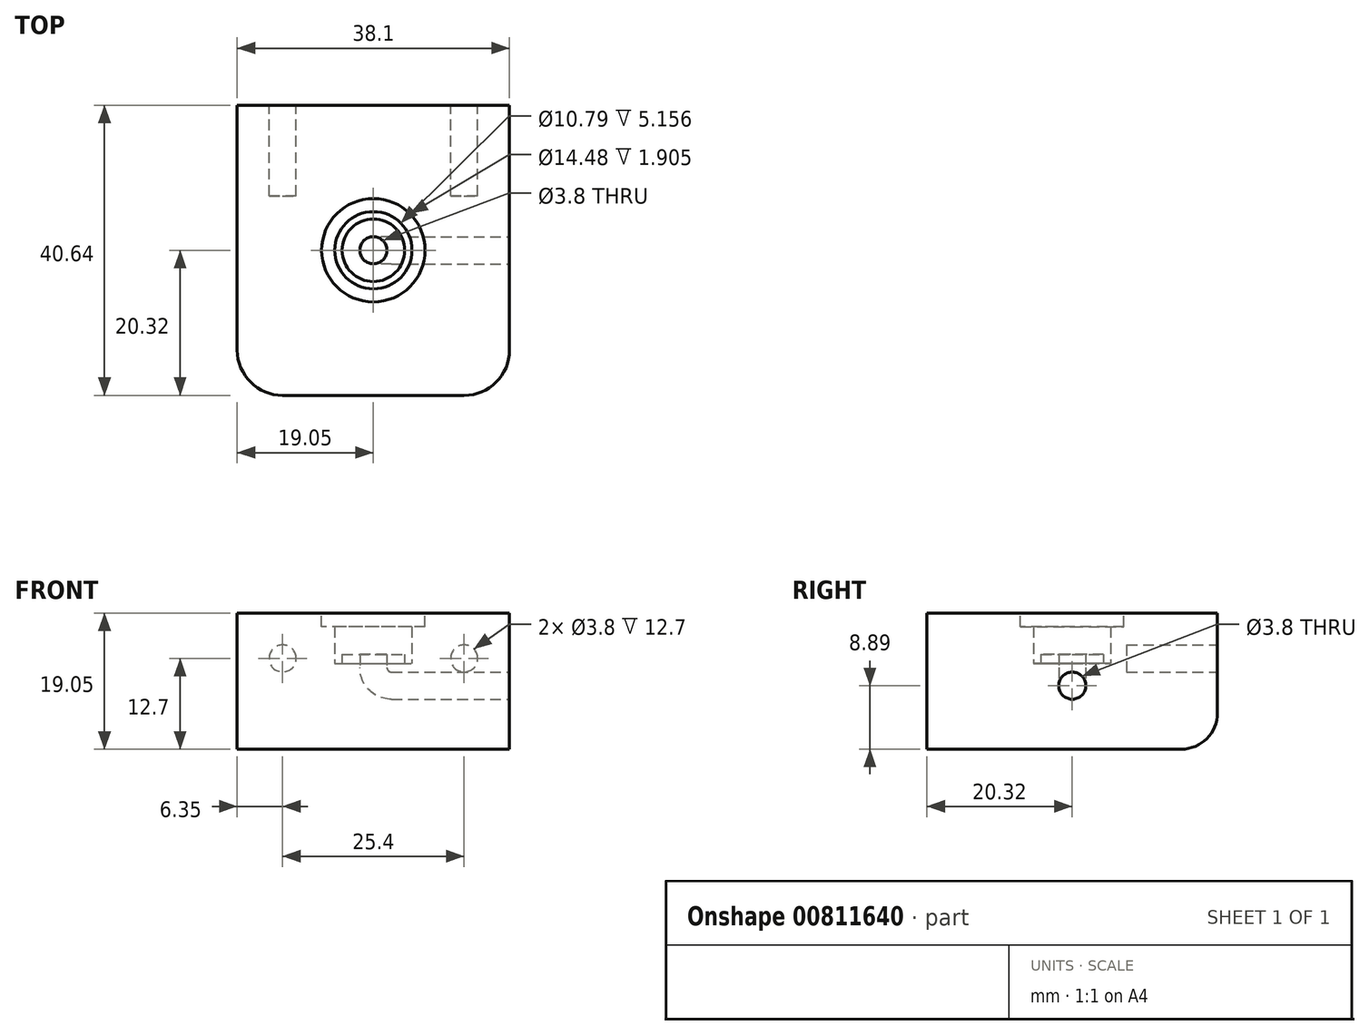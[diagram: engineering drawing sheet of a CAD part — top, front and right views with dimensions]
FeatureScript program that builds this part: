
annotation { "Feature Type Name" : "Feature", "Feature Type Description" : "" }
export const myFeature = defineFeature(function(context is Context, id is Id, definition is map)
    precondition{}
    {
        {
            var Q0;
            Q0=qCreatedBy(makeId("Top.planeOp"),FACE);
            var sketch = newSketch(context, id + "F0", { "sketchPlane" : qUnion([Q0])});
            skLineSegment(sketch, "E0.bottom", {"start": v(19.05, -20.32) * mm, "end": v(-19.05, -20.32) * mm});
            skLineSegment(sketch, "E0.top", {"start": v(19.05, 20.32) * mm, "end": v(-19.05, 20.32) * mm});
            skLineSegment(sketch, "E0.left", {"start": v(19.05, -20.32) * mm, "end": v(19.05, 20.32) * mm});
            skLineSegment(sketch, "E0.right", {"start": v(-19.05, -20.32) * mm, "end": v(-19.05, 20.32) * mm});
            skPoint(sketch, "E0.middle", {"position": v(0, 0) * mm});
            skSolve(sketch);
        }
        {
            var Q0;
            Q0 = qSketchRegion(id + "F0", true);
            extrude(context, id + "F1", {"entities" : qUnion([Q0]), "oppositeDirection" : true, "depth" : 19.05 * mm, "offsetDistance" : 25.4 * mm});
        }
        {
            var Q0;
            Q0=qCreatedBy(makeId("Front.planeOp"),FACE);
            var sketch = newSketch(context, id + "F2", { "sketchPlane" : qUnion([Q0])});
            skLineSegment(sketch, "E1", {"start": v(0, 0) * mm, "end": v(0, -19.05) * mm, "construction": true});
            skLineSegment(sketch, "E2.0", {"start": v(19.05, -19.05) * mm, "end": v(-19.05, -19.05) * mm, "construction": true});
            skLineSegment(sketch, "E3", {"start": v(0, 0) * mm, "end": v(0, -5.8) * mm});
            skLineSegment(sketch, "E4", {"start": v(0, -5.8) * mm, "end": v(4.38, -5.8) * mm});
            skLineSegment(sketch, "E5", {"start": v(4.38, -5.8) * mm, "end": v(4.38, -7.06) * mm});
            skLineSegment(sketch, "E6", {"start": v(4.38, -7.06) * mm, "end": v(5.4, -7.06) * mm});
            skLineSegment(sketch, "E7", {"start": v(5.4, -7.06) * mm, "end": v(5.4, 0) * mm});
            skLineSegment(sketch, "E8", {"start": v(5.4, 0) * mm, "end": v(0, 0) * mm});
            skLineSegment(sketch, "E9", {"start": v(0, -5.8) * mm, "end": v(0, 0) * mm});
            skSolve(sketch);
        }
        {
            var Q0;
            Q0=makeQuery(id+"F2.imprint","IMPRINT",FACE,{"disambiguationData":[TD([[makeQuery(id+"F2.imprint","IMPRINT",EDGE,{"derivedFrom":sQuery(id+"F2.wireOp",EDGE,"E4")}),1.0]])]});
            var Q1;
            Q1=sQuery(id+"F2.wireOp",EDGE,"E1");
            revolve(context, id + "F3", {"operationType" : NewBodyOperationType.REMOVE, "surfaceOperationType" : NewSurfaceOperationType.NEW, "entities" : qUnion([Q0]), "axis" : qUnion([Q1]), "revolveType" : RevolveType.FULL, "oppositeDirection" : true});
        }
        {
            var Q0;
            Q0=makeQuery(id+"F1.opExtrude","CAP_FACE",FACE,{"disambiguationData":[OSD([sQuery(id+"F0.wireOp",EDGE,"E0.bottom"),sQuery(id+"F0.wireOp",EDGE,"E0.top"),sQuery(id+"F0.wireOp",EDGE,"E0.left"),sQuery(id+"F0.wireOp",EDGE,"E0.right")])],"isStart":true});
            var sketch = newSketch(context, id + "F4", { "sketchPlane" : qUnion([Q0])});
            skCircle(sketch, "E10", {"center": v(0, 0) * mm, "radius": 7.24 * mm});
            skSolve(sketch);
        }
        {
            var Q0;
            Q0 = qSketchRegion(id + "F4", true);
            extrude(context, id + "F5", {"entities" : qUnion([Q0]), "operationType" : NewBodyOperationType.REMOVE, "oppositeDirection" : true, "depth" : 1.9 * mm, "offsetDistance" : 25.4 * mm});
        }
        {
            var Q0;
            Q0=makeQuery(id+"F1.opExtrude","SWEPT_EDGE",EDGE,{"disambiguationData":[OSD([sQuery(id+"F0.wireOp",EDGE,"E0.bottom"),sQuery(id+"F0.wireOp",EDGE,"E0.right")])]});
            var Q1;
            Q1=makeQuery(id+"F1.opExtrude","SWEPT_EDGE",EDGE,{"disambiguationData":[OSD([sQuery(id+"F0.wireOp",EDGE,"E0.bottom"),sQuery(id+"F0.wireOp",EDGE,"E0.left")])]});
            fillet(context, id + "F6", {"entities" : qUnion([Q0, Q1]), "radius" : 6.35 * mm, "tangentPropagation" : true, "allowEdgeOverflow" : false});
        }
        {
            var Q0;
            Q0=qCreatedBy(makeId("Front.planeOp"),FACE);
            var sketch = newSketch(context, id + "F7", { "sketchPlane" : qUnion([Q0])});
            skLineSegment(sketch, "E11.0", {"start": v(4.38, -5.8) * mm, "end": v(-4.38, -5.8) * mm, "construction": true});
            skLineSegment(sketch, "E12.0", {"start": v(19.05, 0) * mm, "end": v(19.05, -19.05) * mm, "construction": true});
            skLineSegment(sketch, "E13", {"start": v(0, -5.8) * mm, "end": v(0, -7.62) * mm});
            skLineSegment(sketch, "E14", {"start": v(2.54, -10.16) * mm, "end": v(19.05, -10.16) * mm});
            skPoint(sketch, "E15.visualSharp", {"position": v(0, -10.16) * mm});
            skArc(sketch, "E15.filletArc", {"start": v(0, -7.62) * mm, "mid": v(0.74, -9.42) * mm, "end": v(2.54, -10.16) * mm});
            skSolve(sketch);
        }
        {
            var Q0;
            Q0=makeQuery(id+"F3.boolean.opBoolean","COPY",FACE,{"derivedFrom":makeQuery(id+"F3.opRevolve","SWEPT_FACE",FACE,{"disambiguationData":[OSD([sQuery(id+"F2.wireOp",EDGE,"E4")])]})});
            var sketch = newSketch(context, id + "F8", { "sketchPlane" : qUnion([Q0])});
            skCircle(sketch, "E16", {"center": v(0, 0) * mm, "radius": 1.9 * mm});
            skSolve(sketch);
        }
        {
            var Q0;
            Q0=makeQuery(id+"F8.imprint","IMPRINT",FACE,{"disambiguationData":[TD([[makeQuery(id+"F8.imprint","IMPRINT",EDGE,{"derivedFrom":sQuery(id+"F8.wireOp",EDGE,"E16")}),1.0]])]});
            var Q1;
            Q1=sQuery(id+"F8.wireOp",EDGE,"E16");
            var Q2;
            Q2=sQuery(id+"F7.wireOp",EDGE,"E13");
            var Q3;
            Q3=sQuery(id+"F7.wireOp",EDGE,"E15.filletArc");
            var Q4;
            Q4=sQuery(id+"F7.wireOp",EDGE,"E14");
            sweep(context, id + "F9", {"operationType" : NewBodyOperationType.REMOVE, "profiles" : qUnion([Q0]), "surfaceProfiles" : qUnion([Q1]), "path" : qUnion([Q2, Q3, Q4])});
        }
        {
            var Q0;
            Q0=makeQuery(id+"F1.opExtrude","SWEPT_FACE",FACE,{"disambiguationData":[OSD([sQuery(id+"F0.wireOp",EDGE,"E0.top")])]});
            var sketch = newSketch(context, id + "F10", { "sketchPlane" : qUnion([Q0])});
            skLineSegment(sketch, "E17", {"start": v(0, 0) * mm, "end": v(0, -19.05) * mm, "construction": true});
            skLineSegment(sketch, "E18", {"start": v(-19.05, -9.53) * mm, "end": v(19.05, -9.53) * mm, "construction": true});
            skLineSegment(sketch, "E19.bottom", {"start": v(12.7, -12.7) * mm, "end": v(-12.7, -12.7) * mm, "construction": true});
            skLineSegment(sketch, "E19.top", {"start": v(12.7, -6.35) * mm, "end": v(-12.7, -6.35) * mm, "construction": true});
            skLineSegment(sketch, "E19.left", {"start": v(12.7, -12.7) * mm, "end": v(12.7, -6.35) * mm, "construction": true});
            skLineSegment(sketch, "E19.right", {"start": v(-12.7, -12.7) * mm, "end": v(-12.7, -6.35) * mm, "construction": true});
            skPoint(sketch, "E19.middle", {"position": v(0, -9.53) * mm});
            skCircle(sketch, "E20", {"center": v(-12.7, -6.35) * mm, "radius": 1.9 * mm});
            skCircle(sketch, "E21", {"center": v(12.7, -6.35) * mm, "radius": 1.9 * mm});
            skSolve(sketch);
        }
        {
            var Q0;
            Q0 = qSketchRegion(id + "F10", true);
            extrude(context, id + "F11", {"entities" : qUnion([Q0]), "operationType" : NewBodyOperationType.REMOVE, "oppositeDirection" : true, "depth" : 12.7 * mm, "offsetDistance" : 25.4 * mm});
        }
        {
            var Q0;
            Q0=makeQuery(id+"F1.opExtrude","CAP_EDGE",EDGE,{"disambiguationData":[OSD([sQuery(id+"F0.wireOp",EDGE,"E0.top")])],"isStart":false});
            fillet(context, id + "F12", {"entities" : qUnion([Q0]), "radius" : 5.08 * mm, "tangentPropagation" : true, "allowEdgeOverflow" : false});
        }
    });
